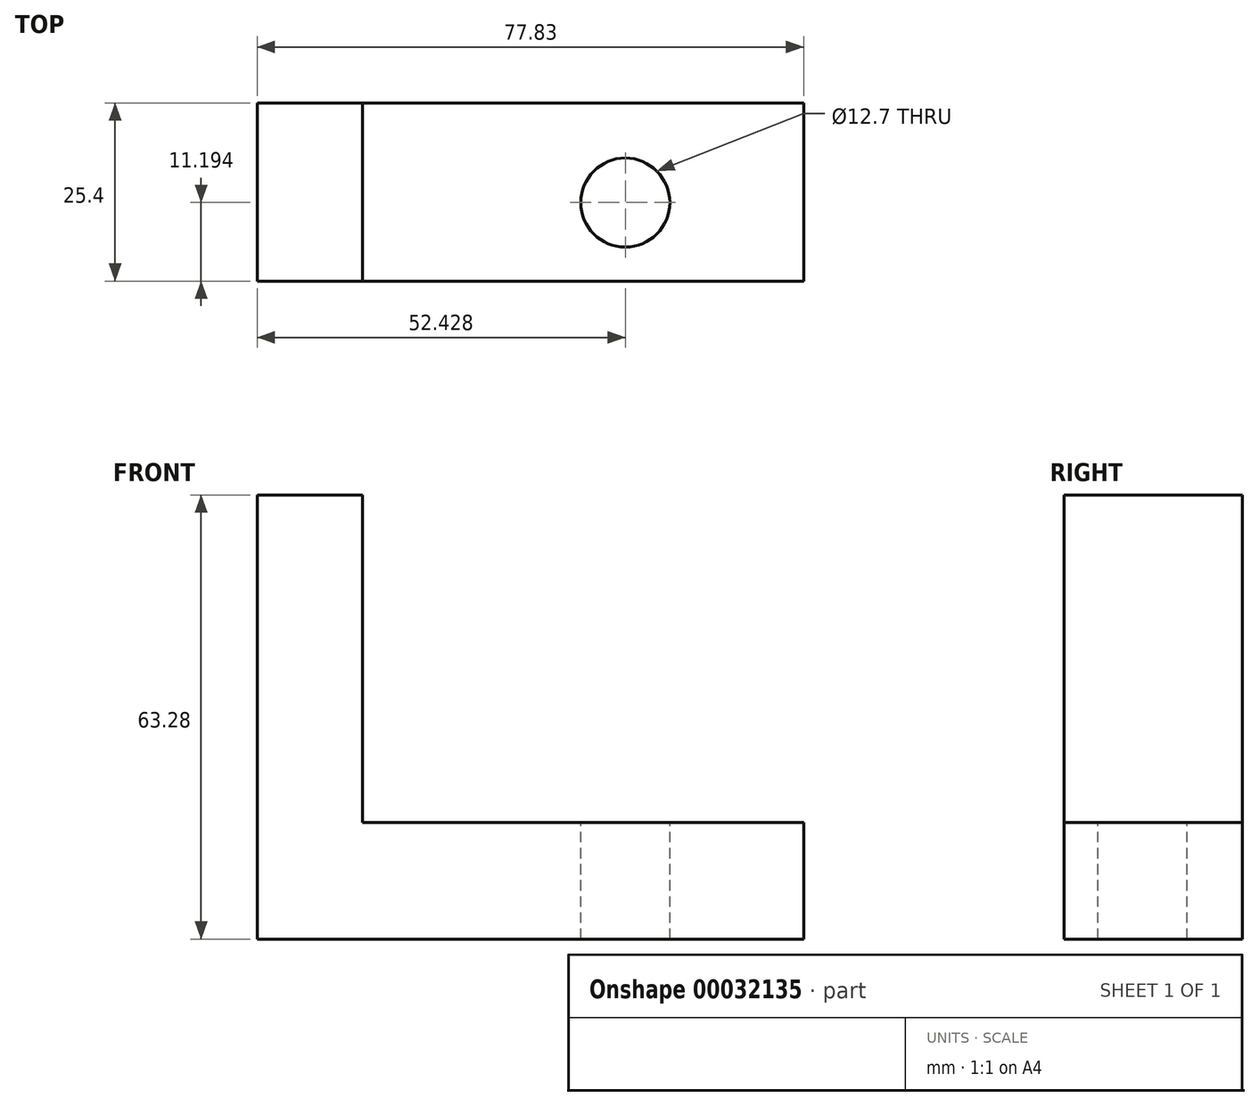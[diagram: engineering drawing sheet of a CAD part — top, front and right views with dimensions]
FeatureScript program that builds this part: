
annotation { "Feature Type Name" : "Feature", "Feature Type Description" : "" }
export const myFeature = defineFeature(function(context is Context, id is Id, definition is map)
    precondition{}
    {
        {
            var Q0;
            Q0=qCreatedBy(makeId("Front.planeOp"),FACE);
            var sketch = newSketch(context, id + "F0", { "sketchPlane" : qUnion([Q0])});
            skLineSegment(sketch, "E0.bottom", {"start": v(-43.75, 39.52) * mm, "end": v(-28.74, 39.52) * mm});
            skLineSegment(sketch, "E0.top", {"start": v(-43.75, -23.76) * mm, "end": v(-28.74, -23.76) * mm});
            skLineSegment(sketch, "E0.left", {"start": v(-43.75, 39.52) * mm, "end": v(-43.75, -23.76) * mm});
            skLineSegment(sketch, "E0.right", {"start": v(-28.74, 39.52) * mm, "end": v(-28.74, -7.13) * mm});
            skLineSegment(sketch, "E1.bottom", {"start": v(-28.74, -7.13) * mm, "end": v(34.08, -7.13) * mm});
            skLineSegment(sketch, "E1.top", {"start": v(-28.74, -23.76) * mm, "end": v(34.08, -23.76) * mm});
            skLineSegment(sketch, "E1.right", {"start": v(34.08, -7.13) * mm, "end": v(34.08, -23.76) * mm});
            skSolve(sketch);
        }
        {
            var Q0;
            Q0=makeQuery(id+"F0.imprint","IMPRINT",FACE,{"disambiguationData":[TD([[makeQuery(id+"F0.imprint","IMPRINT",EDGE,{"derivedFrom":sQuery(id+"F0.wireOp",EDGE,"E0.bottom")}),-1.0]])]});
            extrude(context, id + "F1", {"entities" : qUnion([Q0]), "depth" : 25.4 * mm});
        }
        {
            var Q0;
            Q0=makeQuery(id+"F1.opExtrude","SWEPT_FACE",FACE,{"disambiguationData":[OSD([sQuery(id+"F0.wireOp",EDGE,"E1.bottom")])]});
            var sketch = newSketch(context, id + "F2", { "sketchPlane" : qUnion([Q0])});
            skCircle(sketch, "E2", {"center": v(8.68, -14.2) * mm, "radius": 6.35 * mm});
            skSolve(sketch);
        }
        {
            var Q0;
            Q0=makeQuery(id+"F2.imprint","IMPRINT",FACE,{"disambiguationData":[TD([[makeQuery(id+"F2.imprint","IMPRINT",EDGE,{"derivedFrom":sQuery(id+"F2.wireOp",EDGE,"E2")}),1.0]])]});
            extrude(context, id + "F3", {"entities" : qUnion([Q0]), "operationType" : NewBodyOperationType.REMOVE, "oppositeDirection" : true, "depth" : 25.4 * mm});
        }
    });
